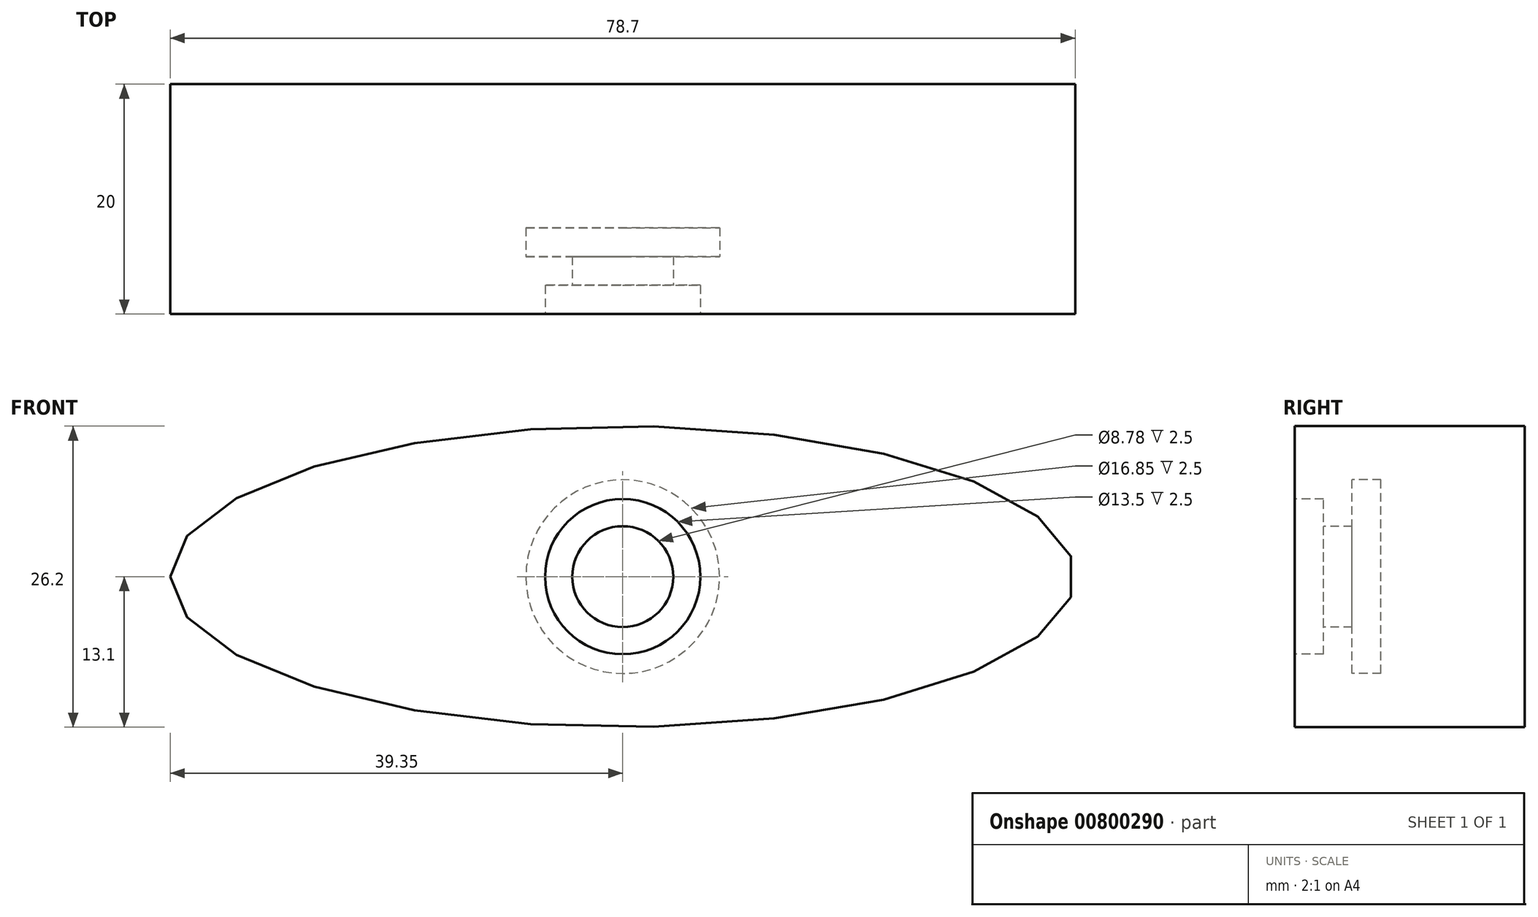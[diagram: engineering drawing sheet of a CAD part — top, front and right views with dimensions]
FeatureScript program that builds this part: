
annotation { "Feature Type Name" : "Feature", "Feature Type Description" : "" }
export const myFeature = defineFeature(function(context is Context, id is Id, definition is map)
    precondition{}
    {
        {
            var Q0;
            Q0=qCreatedBy(makeId("Front.planeOp"),FACE);
            var sketch = newSketch(context, id + "F0", { "sketchPlane" : qUnion([Q0])});
            skEllipse(sketch, "E0", {"center": v(0, 0) * mm, "majorRadius": 39.35 * mm, "minorRadius": 13.1 * mm, "majorAxis": v(-1, 0)});
            skSolve(sketch);
        }
        {
            var Q0;
            Q0=makeQuery(id+"F0.imprint","IMPRINT",FACE,{"disambiguationData":[TD([[makeQuery(id+"F0.imprint","IMPRINT",EDGE,{"derivedFrom":sQuery(id+"F0.wireOp",EDGE,"E0")}),1.0]])]});
            extrude(context, id + "F1", {"entities" : qUnion([Q0]), "depth" : 20 * mm, "offsetDistance" : 25 * mm});
        }
        {
            var Q0;
            Q0=makeQuery(id+"F1.opExtrude","CAP_FACE",FACE,{"disambiguationData":[OSD([sQuery(id+"F0.wireOp",EDGE,"E0")])],"isStart":false});
            var sketch = newSketch(context, id + "F2", { "sketchPlane" : qUnion([Q0])});
            skCircle(sketch, "E1", {"center": v(0, 0) * mm, "radius": 4.39 * mm});
            skSolve(sketch);
        }
        {
            var Q0;
            Q0=makeQuery(id+"F2.imprint","IMPRINT",FACE,{"disambiguationData":[TD([[makeQuery(id+"F2.imprint","IMPRINT",EDGE,{"derivedFrom":sQuery(id+"F2.wireOp",EDGE,"E1")}),1.0]])]});
            extrude(context, id + "F3", {"entities" : qUnion([Q0]), "operationType" : NewBodyOperationType.REMOVE, "oppositeDirection" : true, "depth" : 5 * mm, "offsetDistance" : 25 * mm});
        }
        {
            var Q0;
            Q0=makeQuery(id+"F3.boolean.opBoolean","COPY",FACE,{"derivedFrom":makeQuery(id+"F3.opExtrude","CAP_FACE",FACE,{"disambiguationData":[OSD([sQuery(id+"F2.wireOp",EDGE,"E1")])],"isStart":false})});
            var sketch = newSketch(context, id + "F4", { "sketchPlane" : qUnion([Q0])});
            skCircle(sketch, "E2", {"center": v(0, 0) * mm, "radius": 8.42 * mm});
            skSolve(sketch);
        }
        {
            var Q0;
            Q0 = qSketchRegion(id + "F4", true);
            extrude(context, id + "F5", {"entities" : qUnion([Q0]), "operationType" : NewBodyOperationType.REMOVE, "oppositeDirection" : true, "depth" : 2.5 * mm, "offsetDistance" : 25 * mm});
        }
        {
            var Q0;
            Q0=makeQuery(id+"F1.opExtrude","CAP_FACE",FACE,{"disambiguationData":[OSD([sQuery(id+"F0.wireOp",EDGE,"E0")])],"isStart":false});
            var sketch = newSketch(context, id + "F6", { "sketchPlane" : qUnion([Q0])});
            skCircle(sketch, "E3", {"center": v(0, 0) * mm, "radius": 6.75 * mm});
            skSolve(sketch);
        }
        {
            var Q0;
            Q0 = qSketchRegion(id + "F6", true);
            extrude(context, id + "F7", {"entities" : qUnion([Q0]), "operationType" : NewBodyOperationType.REMOVE, "oppositeDirection" : true, "depth" : 2.5 * mm, "offsetDistance" : 25 * mm});
        }
    });
